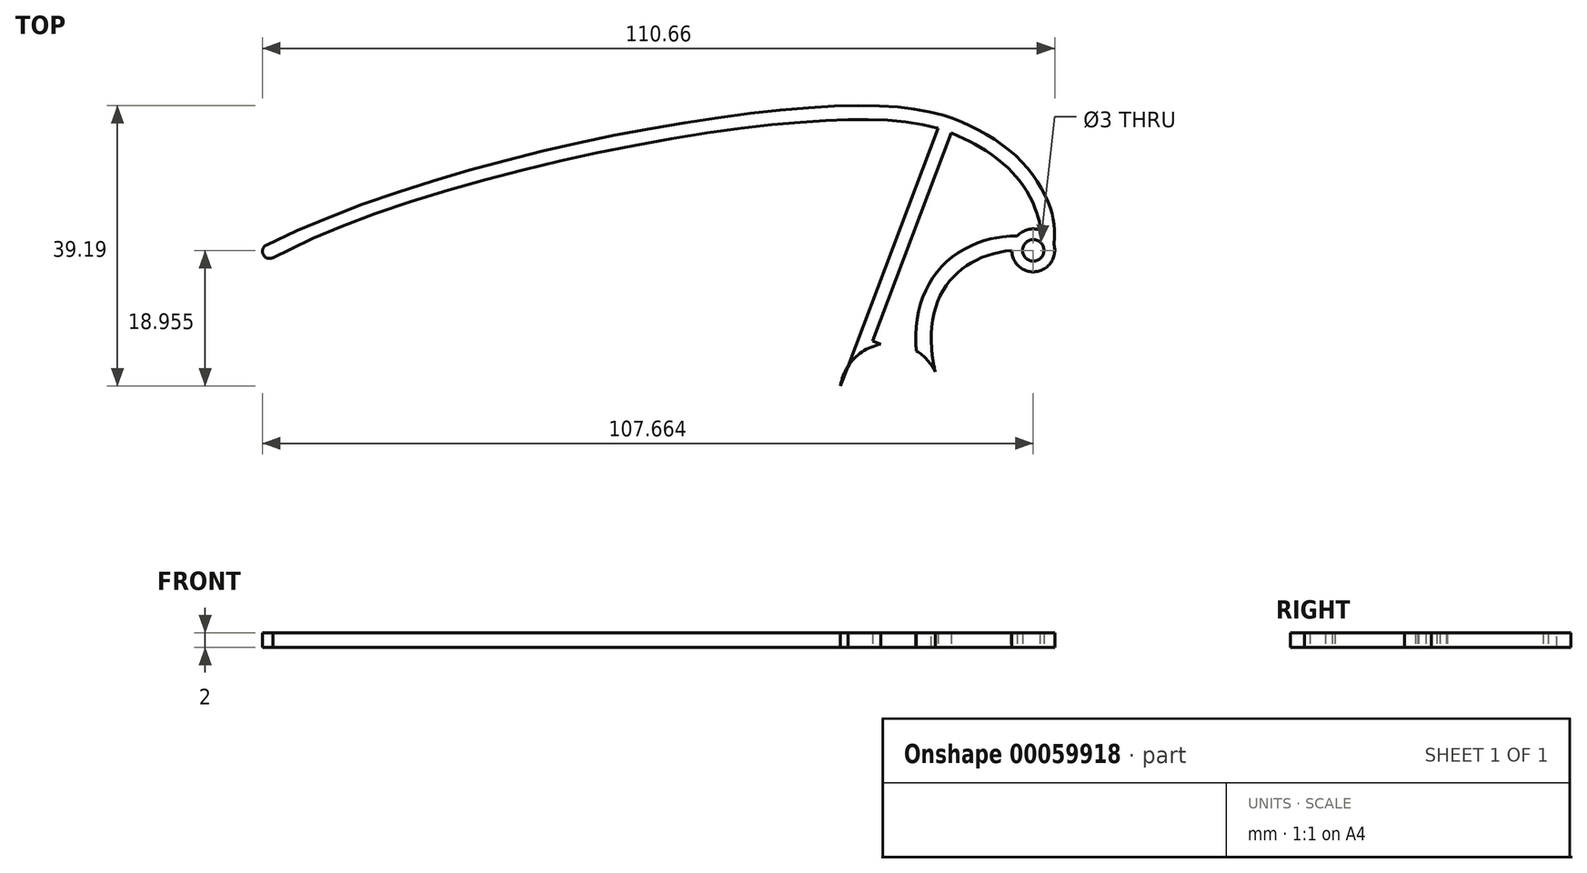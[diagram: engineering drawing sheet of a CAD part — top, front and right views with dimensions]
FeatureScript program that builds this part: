
annotation { "Feature Type Name" : "Feature", "Feature Type Description" : "" }
export const myFeature = defineFeature(function(context is Context, id is Id, definition is map)
    precondition{}
    {
        {
            var Q0;
            Q0=qCreatedBy(makeId("Top.planeOp"),FACE);
            var sketch = newSketch(context, id + "F0", { "sketchPlane" : qUnion([Q0])});
            skCircle(sketch, "E0", {"center": v(35.3, -60.7) * mm, "radius": 5 * mm});
            skLineSegment(sketch, "E1.0", {"start": v(32.55, -54.26) * mm, "end": v(32.55, -54.26) * mm});
            skCircle(sketch, "E2", {"center": v(55.3, -40.7) * mm, "radius": 1.5 * mm});
            skCircle(sketch, "E3.0", {"center": v(55.3, -40.7) * mm, "radius": 3 * mm});
            skFitSpline(sketch, "E4", {"points": [v(58.2, -39.93) * mm, v(57.85, -35.33) * mm, v(54.71, -29.46) * mm, v(47.3, -23.7) * mm, v(30.2, -20.46) * mm, v(-51.8, -39.93) * mm], "startDerivative": vector(3.26, 64.81) * mm, "endDerivative": vector(-169.57, -83.15) * mm});
            skFitSpline(sketch, "E5", {"points": [v(52.3, -40.7) * mm, v(42.26, -59.99) * mm], "startDerivative": vector(-24.7, -2.31) * mm, "endDerivative": vector(11.54, -35.37) * mm});
            skLineSegment(sketch, "E6", {"start": v(41.09, -54.44) * mm, "end": v(-19.98, -30.6) * mm});
            skLineSegment(sketch, "E7", {"start": v(28.37, -59.65) * mm, "end": v(42.67, -21.81) * mm});
            skFitSpline(sketch, "E8.0", {"points": [v(56.2, -39.82) * mm, v(56.23, -39.17) * mm, v(56.26, -38.37) * mm, v(56.24, -37.58) * mm, v(56.18, -36.92) * mm, v(56.07, -36.35) * mm, v(55.85, -35.63) * mm, v(55.57, -34.83) * mm, v(55.08, -33.7) * mm, v(54.3, -32.3) * mm, v(53.5, -31.13) * mm, v(52.78, -30.26) * mm, v(52, -29.4) * mm, v(50.9, -28.4) * mm, v(49.4, -27.26) * mm, v(48.04, -26.38) * mm, v(46.9, -25.74) * mm, v(45.71, -25.12) * mm, v(44.2, -24.43) * mm, v(42.24, -23.73) * mm, v(40, -23.17) * mm, v(37.4, -22.75) * mm, v(34.35, -22.5) * mm, v(30.75, -22.42) * mm, v(26.51, -22.57) * mm, v(20.11, -23.03) * mm, v(10.91, -24.12) * mm, v(-1.4, -26.22) * mm, v(-14.4, -29.06) * mm, v(-27.44, -32.6) * mm, v(-39.92, -36.81) * mm, v(-47.46, -40.03) * mm, v(-50.93, -41.73) * mm]});
            skArc(sketch, "E9", {"start": v(-51.8, -39.93) * mm, "mid": v(-52.26, -41.27) * mm, "end": v(-50.93, -41.73) * mm});
            skLineSegment(sketch, "E10.0", {"start": v(33.99, -53.82) * mm, "end": v(-23.2, -31.5) * mm});
            skLineSegment(sketch, "E11.0", {"start": v(30.24, -60.36) * mm, "end": v(31.2, -57.82) * mm});
            skFitSpline(sketch, "E12.0", {"points": [v(52.1, -38.7) * mm, v(50.95, -38.82) * mm, v(48.72, -39.24) * mm, v(45.66, -40.53) * mm, v(43, -42.48) * mm, v(40.92, -45.08) * mm, v(39.52, -48.26) * mm, v(38.9, -51.94) * mm, v(39.12, -56.04) * mm, v(39.84, -59.04) * mm, v(40.36, -60.6) * mm]});
            skFitSpline(sketch, "E13.trimOffspring", {"points": [v(52.1, -38.7) * mm, v(50.95, -38.82) * mm, v(48.72, -39.24) * mm, v(45.66, -40.53) * mm, v(43, -42.48) * mm, v(40.92, -45.08) * mm, v(39.52, -48.26) * mm, v(38.9, -51.94) * mm, v(39.12, -56.04) * mm, v(39.84, -59.04) * mm, v(40.36, -60.6) * mm]});
            skLineSegment(sketch, "E14.trimOffspring", {"start": v(32.55, -54.26) * mm, "end": v(44.54, -22.52) * mm});
            skCircle(sketch, "E15.converted", {"center": v(35.3, -60.7) * mm, "radius": 7 * mm});
            skFitSpline(sketch, "E16", {"points": [v(52.1, -38.7) * mm, v(53.05, -38.7) * mm], "startDerivative": vector(0.94, 0) * mm, "endDerivative": vector(0.94, 0) * mm});
            skSolve(sketch);
        }
        {
            var Q0;
            {var subQ0=sQuery(id+"F0.wireOp",EDGE,"E15.converted");var subQ1=sQuery(id+"F0.wireOp",EDGE,"E7");var subQ2=makeQuery(id+"F0.imprint","INTERSECT",VERTEX,{"disambiguationData":[OD(0.0)],"derivedFrom":[subQ1,subQ0]});Q0=makeQuery(id+"F0.imprint","IMPRINT",FACE,{"disambiguationData":[TD([[makeQuery(id+"F0.imprint","IMPRINT",EDGE,{"disambiguationData":[TD([[subQ2,-1.0]])],"derivedFrom":subQ1}),1.0]])]});}
            var Q1;
            {var subQ5=sQuery(id+"F0.wireOp",EDGE,"E9");Q1=makeQuery(id+"F0.imprint","IMPRINT",FACE,{"disambiguationData":[TD([[makeQuery(id+"F0.imprint","IMPRINT",EDGE,{"derivedFrom":subQ5}),1.0]])]});}
            var Q2;
            Q2=makeQuery(id+"F0.imprint","IMPRINT",FACE,{"disambiguationData":[TD([[makeQuery(id+"F0.imprint","IMPRINT",EDGE,{"derivedFrom":sQuery(id+"F0.wireOp",EDGE,"E2")}),-1.0]])]});
            var Q3;
            {var subQ0=sQuery(id+"F0.wireOp",EDGE,"E6");var subQ1=sQuery(id+"F0.wireOp",EDGE,"E4");var subQ2=makeQuery(id+"F0.imprint","INTERSECT",VERTEX,{"derivedFrom":[subQ1,subQ0]});Q3=makeQuery(id+"F0.imprint","IMPRINT",FACE,{"disambiguationData":[TD([[makeQuery(id+"F0.imprint","IMPRINT",EDGE,{"disambiguationData":[TD([[subQ2,1.0]])],"derivedFrom":subQ1}),1.0]])]});}
            var Q4;
            {var subQ0=sQuery(id+"F0.wireOp",EDGE,"E7");var subQ1=sQuery(id+"F0.wireOp",EDGE,"E6");var subQ2=makeQuery(id+"F0.imprint","INTERSECT",VERTEX,{"derivedFrom":[subQ1,subQ0]});Q4=makeQuery(id+"F0.imprint","IMPRINT",FACE,{"disambiguationData":[TD([[makeQuery(id+"F0.imprint","IMPRINT",EDGE,{"disambiguationData":[TD([[subQ2,-1.0]])],"derivedFrom":subQ1}),1.0]])]});}
            var Q5;
            {var subQ0=sQuery(id+"F0.wireOp",EDGE,"E15.converted");var subQ1=sQuery(id+"F0.wireOp",EDGE,"E7");var subQ2=makeQuery(id+"F0.imprint","INTERSECT",VERTEX,{"disambiguationData":[OD(1.0)],"derivedFrom":[subQ1,subQ0]});Q5=makeQuery(id+"F0.imprint","IMPRINT",FACE,{"disambiguationData":[TD([[makeQuery(id+"F0.imprint","IMPRINT",EDGE,{"disambiguationData":[TD([[subQ2,-1.0]])],"derivedFrom":subQ1}),-1.0]])]});}
            var Q6;
            {var subQ1=sQuery(id+"F0.wireOp",EDGE,"E3.0");var subQ6=sQuery(id+"F0.wireOp",EDGE,"E4");var subQ8=makeQuery(id+"F0.imprint","INTERSECT",VERTEX,{"derivedFrom":[subQ1,subQ6]});Q6=makeQuery(id+"F0.imprint","IMPRINT",FACE,{"disambiguationData":[TD([[makeQuery(id+"F0.imprint","IMPRINT",EDGE,{"disambiguationData":[TD([[subQ8,-1.0]])],"derivedFrom":subQ1}),-1.0]])]});}
            var Q7;
            {var subQ5=sQuery(id+"F0.wireOp",EDGE,"E6");var subQ6=makeQuery(id+"F0.imprint","IMPRINT",VERTEX,{"derivedFrom":subQ5});Q7=makeQuery(id+"F0.imprint","IMPRINT",FACE,{"disambiguationData":[TD([[makeQuery(id+"F0.imprint","IMPRINT",EDGE,{"disambiguationData":[TD([[subQ6,1.0]])],"derivedFrom":subQ5}),1.0]])]});}
            var Q8;
            {var subQ0=sQuery(id+"F0.wireOp",EDGE,"E14.trimOffspring");var subQ1=sQuery(id+"F0.wireOp",EDGE,"E6");var subQ2=makeQuery(id+"F0.imprint","INTERSECT",VERTEX,{"derivedFrom":[subQ1,subQ0]});Q8=makeQuery(id+"F0.imprint","IMPRINT",FACE,{"disambiguationData":[TD([[makeQuery(id+"F0.imprint","IMPRINT",EDGE,{"disambiguationData":[TD([[subQ2,-1.0]])],"derivedFrom":subQ1}),1.0]])]});}
            var Q9;
            {var subQ5=sQuery(id+"F0.wireOp",EDGE,"E0");var subQ6=makeQuery(id+"F0.imprint","IMPRINT",VERTEX,{"derivedFrom":subQ5});Q9=makeQuery(id+"F0.imprint","IMPRINT",FACE,{"disambiguationData":[TD([[makeQuery(id+"F0.imprint","IMPRINT",EDGE,{"disambiguationData":[TD([[subQ6,-1.0]])],"derivedFrom":subQ5}),-1.0]])]});}
            var Q10;
            {var subQ0=sQuery(id+"F0.wireOp",EDGE,"E14.trimOffspring");var subQ1=sQuery(id+"F0.wireOp",EDGE,"E6");var subQ2=makeQuery(id+"F0.imprint","INTERSECT",VERTEX,{"derivedFrom":[subQ1,subQ0]});Q10=makeQuery(id+"F0.imprint","IMPRINT",FACE,{"disambiguationData":[TD([[makeQuery(id+"F0.imprint","IMPRINT",EDGE,{"disambiguationData":[TD([[subQ2,-1.0]])],"derivedFrom":subQ1}),-1.0]])]});}
            var Q11;
            {var subQ0=sQuery(id+"F0.wireOp",EDGE,"E16");Q11=makeQuery(id+"F0.imprint","IMPRINT",FACE,{"disambiguationData":[TD([[makeQuery(id+"F0.imprint","IMPRINT",EDGE,{"derivedFrom":subQ0}),-1.0]])]});}
            var Q12;
            {var subQ0=sQuery(id+"F0.wireOp",EDGE,"E15.converted");var subQ8=sQuery(id+"F0.wireOp",EDGE,"E5");var subQ10=makeQuery(id+"F0.imprint","INTERSECT",VERTEX,{"derivedFrom":[subQ8,subQ0]});Q12=makeQuery(id+"F0.imprint","IMPRINT",FACE,{"disambiguationData":[TD([[makeQuery(id+"F0.imprint","IMPRINT",EDGE,{"disambiguationData":[TD([[subQ10,1.0]])],"derivedFrom":subQ8}),-1.0]])]});}
            var Q13;
            {var subQ0=sQuery(id+"F0.wireOp",EDGE,"E15.converted");var subQ1=sQuery(id+"F0.wireOp",EDGE,"E10.0");var subQ2=makeQuery(id+"F0.imprint","INTERSECT",VERTEX,{"derivedFrom":[subQ1,subQ0]});Q13=makeQuery(id+"F0.imprint","IMPRINT",FACE,{"disambiguationData":[TD([[makeQuery(id+"F0.imprint","IMPRINT",EDGE,{"disambiguationData":[TD([[subQ2,-1.0]])],"derivedFrom":subQ1}),1.0]])]});}
            extrude(context, id + "F1", {"entities" : qUnion([Q0, Q1, Q2, Q3, Q4, Q5, Q6, Q7, Q8, Q9, Q10, Q11, Q12, Q13]), "depth" : 2 * mm});
        }
    });
